# Revit family: GRIFO BAÑO-DUCHA EMPOTRABLE KILY
name_source: partatom
category: Aparatos sanitarios
revit_build: Autodesk Revit 2015 (Build: 20140223_1515(x64)
units: mm (PartAtom-declared; Revit-internal decimal feet)

## types (1)
- 4957400
    Accionamiento = Por maneta
    CAUDAL = 11 l/min a 3 bar
    Comentarios de tipo = Mecanismo monomando de baño ducha empotrable.
◦Acabado Cromo
◦Cartucho con discos cerámicos de diámetro 25 mm.
    Conexión AC = Sí
    Conexión AF = Sí
    Código de montaje = C1030220
    Descripción = Mecanismo monomando de baño-ducha Kily. Colección de líneas refinadas y elegantes que se adaptan a todo tipo de ambientes. Su original maneta de forma ondulada destaca en inclinación del escultural diseño del cuerpo del grifo. Una grifería que decora el espacio de baño con personalidad siendo piezas prácticas y ergonómicas muy confortables con el toque de distinción perfecto.
    ENTRADA = Hembra 1/2''
    Elevación por defecto = 1219 mm
    Fabricante = PRESTO IBÉRICA
    Imagen de tipo = <Ninguno>
    Material = LATON CROMADO
    Modelo = KILY
    REFERENCIA = 4957400
    Teléfono = (+34) 915 782 575
    URL = http://www.griferiasgalindo.com
